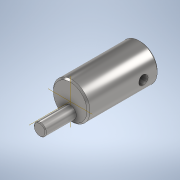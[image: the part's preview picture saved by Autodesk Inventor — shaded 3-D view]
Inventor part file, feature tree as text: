
AUTODESK INVENTOR PART (.ipt)
format: ipt  version: 2021.1 (Build 251245000, 245)  size: 140,800 bytes
history: native  units: in
note: dims shown in document units (in); Inventor stores cm internally (conversion verified against a paired STEP export)
features: extrude x3, sketch x2, chamfer x2, projected_geometry x2
ambient origin geometry x8: Origin, YZ Plane, XZ Plane, XY Plane, X Axis, Y Axis, Z Axis, Center Point
bodies: Solid1 (feature_tree)
feature tree (9):
  sketch  "Sketch1"  dims[d0=1.2in d1=0.4in]
  extrude  "Extrusion1"  Depth=0.4in
  extrude  "Extrusion2"  Depth=2.3in TaperAngle=0.0deg
  extrude  "Extrusion3"  Depth=0.025in TaperAngle=0.0deg
  chamfer  "Chamfer1"  Distance=0.3in
  chamfer  "Chamfer2"  Distance=0.5in
  sketch  "Sketch2"  dims[d2=0.3in d3=2.3in d4=0.0in d5=1.0in d6=0.0in d7=0.3in d8=0.5in d9=0.0in d10=0.0in d11=0.025in d12=0.125in d13=45.0deg d14=0.05in d15=0.125in d16=45.0deg]
  projected_geometry  "Projected Loop1"
  projected_geometry  "Project Cut Edges1"
